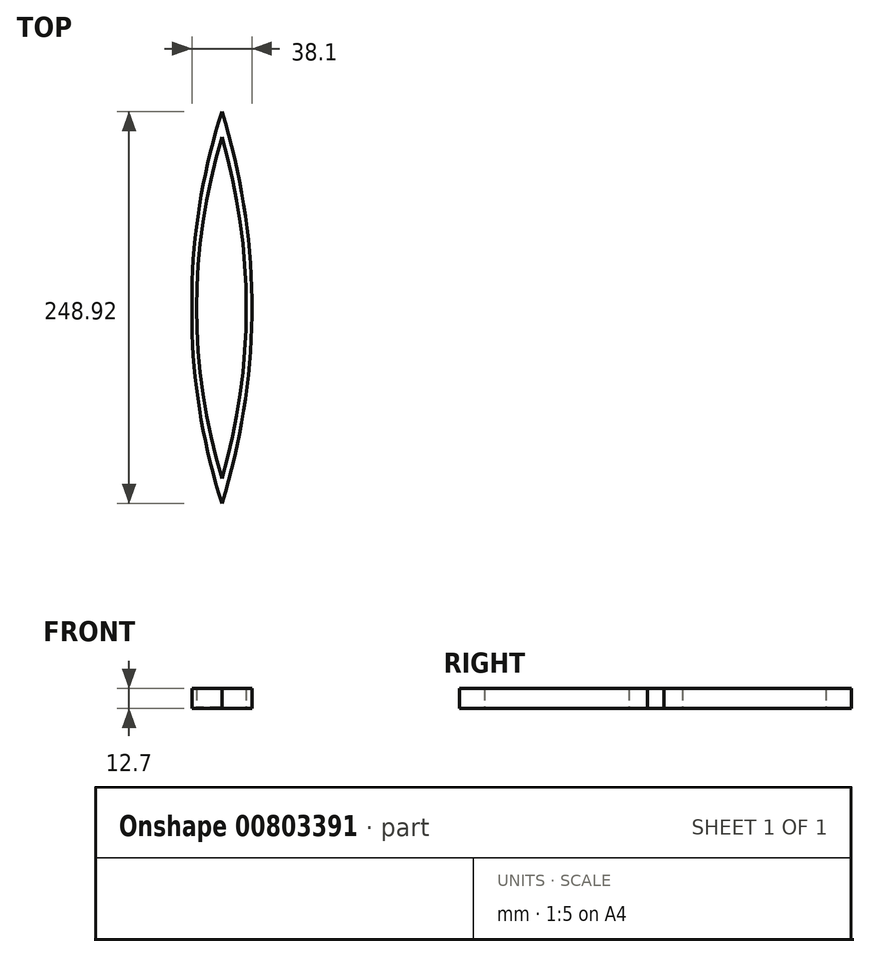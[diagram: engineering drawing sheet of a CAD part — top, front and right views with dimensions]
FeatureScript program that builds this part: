
annotation { "Feature Type Name" : "Feature", "Feature Type Description" : "" }
export const myFeature = defineFeature(function(context is Context, id is Id, definition is map)
    precondition{}
    {
        {
            var Q0;
            Q0=qCreatedBy(makeId("Top.planeOp"),FACE);
            var sketch = newSketch(context, id + "F0", { "sketchPlane" : qUnion([Q0])});
            skLineSegment(sketch, "E0.bottom", {"start": v(-70.96, -81.78) * mm, "end": v(-32.86, -81.78) * mm});
            skLineSegment(sketch, "E0.top", {"start": v(-70.96, 167.14) * mm, "end": v(-32.86, 167.14) * mm});
            skLineSegment(sketch, "E0.left", {"start": v(-70.96, -81.78) * mm, "end": v(-70.96, 167.14) * mm});
            skLineSegment(sketch, "E0.right", {"start": v(-32.86, -81.78) * mm, "end": v(-32.86, 167.14) * mm});
            skArc(sketch, "E1", {"start": v(-51.9, 167.14) * mm, "mid": v(-71.31, 42.68) * mm, "end": v(-51.9, -81.78) * mm});
            skArc(sketch, "E2", {"start": v(-51.9, -81.78) * mm, "mid": v(-32.83, 42.68) * mm, "end": v(-51.9, 167.14) * mm});
            skArc(sketch, "E3", {"start": v(-51.95, -66.06) * mm, "mid": v(-36.44, 42.36) * mm, "end": v(-51.95, 150.79) * mm});
            skPoint(sketch, "E3.startSnap0", {"position": v(-51.95, 150.79) * mm});
            skArc(sketch, "E4", {"start": v(-51.95, 150.79) * mm, "mid": v(-67.96, 42.36) * mm, "end": v(-51.95, -66.06) * mm});
            skPoint(sketch, "E5.orphan", {"position": v(-47.14, 150.79) * mm});
            skPoint(sketch, "E6.start.orphan", {"position": v(-56.76, 150.79) * mm});
            skPoint(sketch, "E7.end.orphan", {"position": v(-47.31, -66.06) * mm});
            skSolve(sketch);
        }
        {
            var Q0;
            Q0=makeQuery(id+"F0.imprint","IMPRINT",FACE,{"disambiguationData":[TD([[makeQuery(id+"F0.imprint","IMPRINT",EDGE,{"derivedFrom":sQuery(id+"F0.wireOp",EDGE,"E3")}),-1.0]])]});
            extrude(context, id + "F1", {"entities" : qUnion([Q0]), "depth" : 12.7 * mm, "offsetDistance" : 25.4 * mm});
        }
        {
            var Q0;
            Q0=makeQuery(id+"F0.imprint","IMPRINT",FACE,{"disambiguationData":[TD([[makeQuery(id+"F0.imprint","IMPRINT",EDGE,{"derivedFrom":sQuery(id+"F0.wireOp",EDGE,"E3")}),1.0]])]});
            extrude(context, id + "F2", {"entities" : qUnion([Q0]), "operationType" : NewBodyOperationType.ADD, "depth" : 0.8 * mm, "offsetDistance" : 25.4 * mm});
        }
    });
